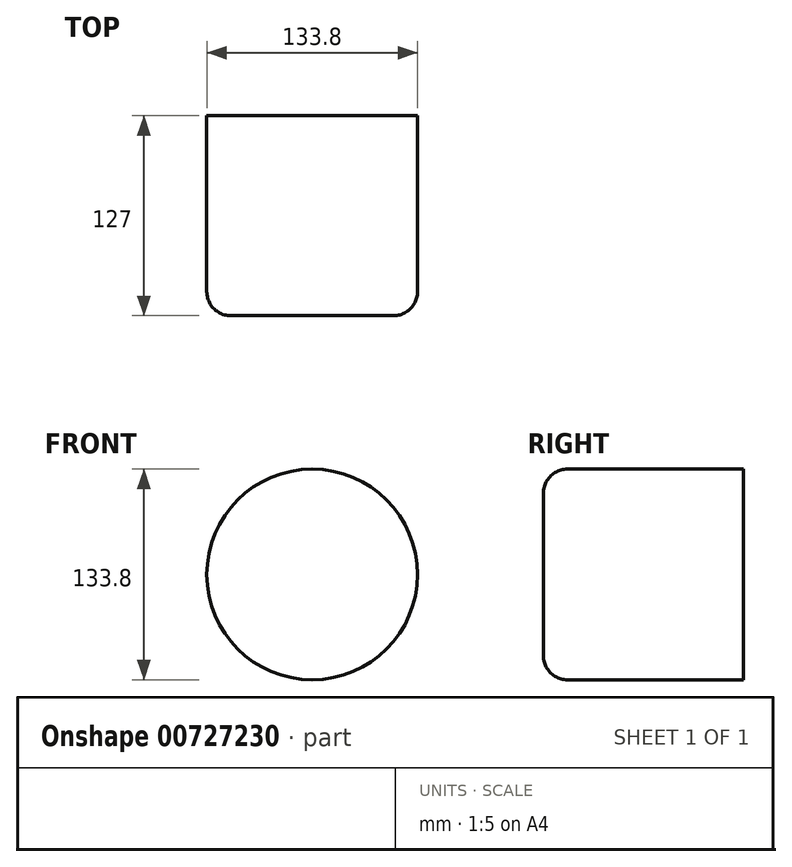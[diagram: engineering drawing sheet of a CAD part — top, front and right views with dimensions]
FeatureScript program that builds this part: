
annotation { "Feature Type Name" : "Feature", "Feature Type Description" : "" }
export const myFeature = defineFeature(function(context is Context, id is Id, definition is map)
    precondition{}
    {
        {
            var Q0;
            Q0=qCreatedBy(makeId("Front.planeOp"),FACE);
            var sketch = newSketch(context, id + "F0", { "sketchPlane" : qUnion([Q0])});
            skCircle(sketch, "E0", {"center": v(0, 0) * mm, "radius": 66.9 * mm});
            skSolve(sketch);
        }
        {
            var Q0;
            Q0 = qSketchRegion(id + "F0", true);
            extrude(context, id + "F1", {"entities" : qUnion([Q0]), "depth" : 127 * mm, "offsetDistance" : 25.4 * mm});
        }
        {
            var Q0;
            Q0=makeQuery(id+"F1.opExtrude","CAP_EDGE",EDGE,{"disambiguationData":[OSD([sQuery(id+"F0.wireOp",EDGE,"E0")])],"isStart":false});
            var Q1;
            Q1=makeQuery(id+"F1.opExtrude","CAP_FACE",FACE,{"disambiguationData":[OSD([sQuery(id+"F0.wireOp",EDGE,"E0")])],"isStart":false});
            fillet(context, id + "F2", {"entities" : qUnion([Q0, Q1]), "radius" : 15.24 * mm, "tangentPropagation" : true, "allowEdgeOverflow" : false});
        }
    });
